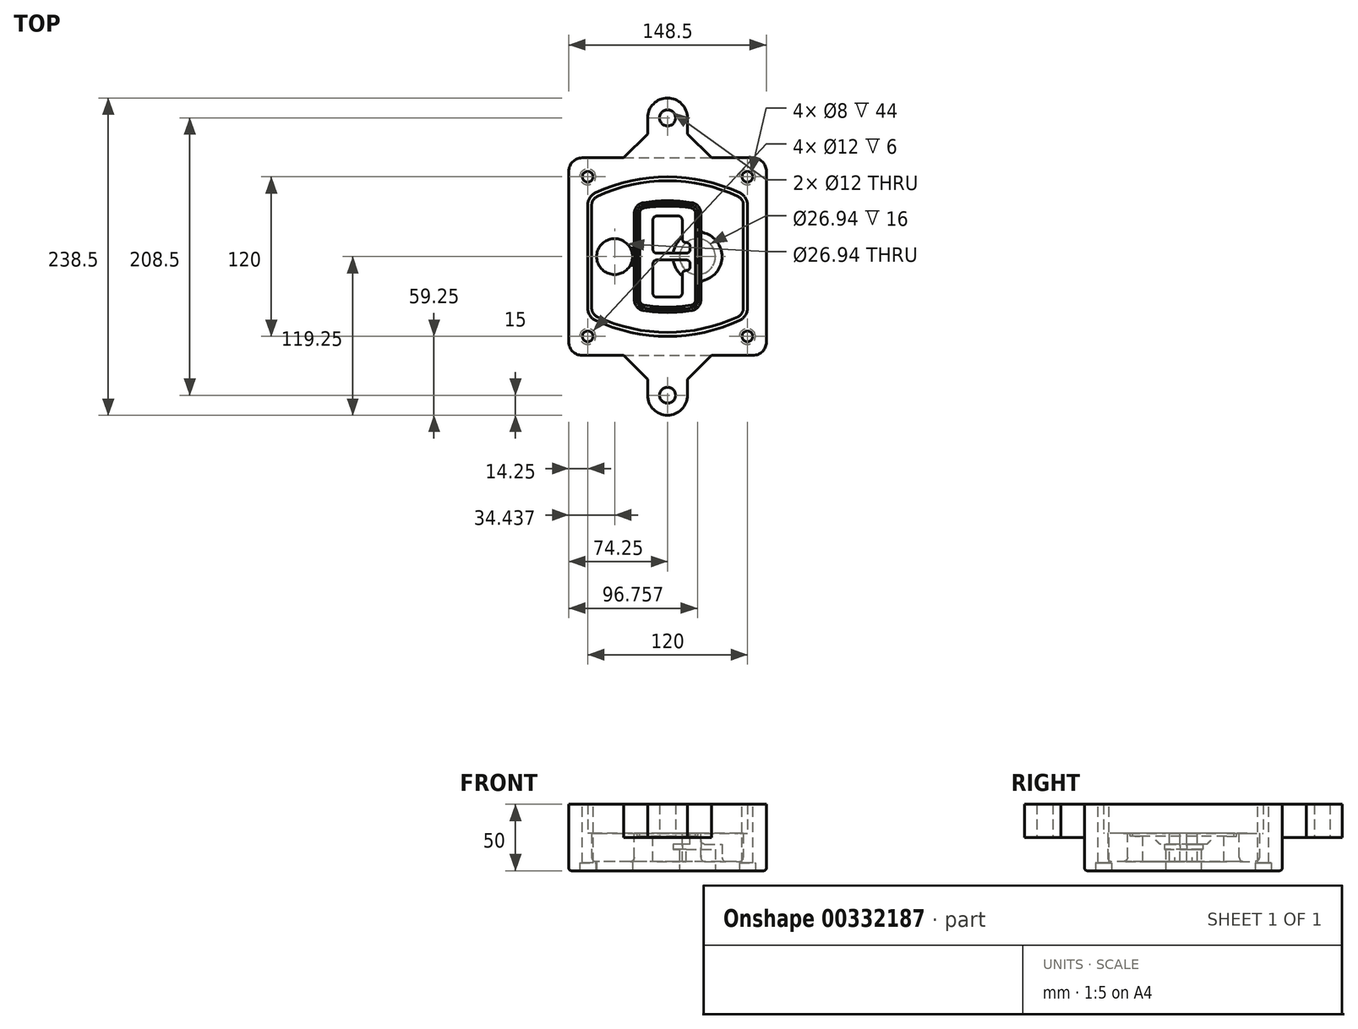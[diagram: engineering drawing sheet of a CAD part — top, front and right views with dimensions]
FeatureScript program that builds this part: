
annotation { "Feature Type Name" : "Feature", "Feature Type Description" : "" }
export const myFeature = defineFeature(function(context is Context, id is Id, definition is map)
    precondition{}
    {
        {
            var Q0;
            Q0=qCreatedBy(makeId("Top.planeOp"),FACE);
            var sketch = newSketch(context, id + "F0", { "sketchPlane" : qUnion([Q0])});
            skPoint(sketch, "E0.rect.middle", {"position": v(0, 0) * mm});
            skLineSegment(sketch, "E1.bottom", {"start": v(-64.25, -74.25) * mm, "end": v(64.25, -74.25) * mm});
            skLineSegment(sketch, "E1.top", {"start": v(-64.25, 74.25) * mm, "end": v(64.25, 74.25) * mm});
            skLineSegment(sketch, "E1.left", {"start": v(-74.25, -64.25) * mm, "end": v(-74.25, 64.25) * mm});
            skLineSegment(sketch, "E1.right", {"start": v(74.25, -64.25) * mm, "end": v(74.25, 64.25) * mm});
            skLineSegment(sketch, "E2", {"start": v(-74.25, 74.25) * mm, "end": v(74.25, -74.25) * mm, "construction": true});
            skLineSegment(sketch, "E3", {"start": v(74.25, 74.25) * mm, "end": v(-74.25, -74.25) * mm, "construction": true});
            skCircle(sketch, "E4", {"center": v(-60, 60) * mm, "radius": 4 * mm});
            skCircle(sketch, "E5", {"center": v(60, 60) * mm, "radius": 4 * mm});
            skCircle(sketch, "E6", {"center": v(60, -60) * mm, "radius": 4 * mm});
            skCircle(sketch, "E7", {"center": v(-60, -60) * mm, "radius": 4 * mm});
            skLineSegment(sketch, "E8", {"start": v(-60, 60) * mm, "end": v(60, 60) * mm, "construction": true});
            skLineSegment(sketch, "E9", {"start": v(60, 60) * mm, "end": v(60, -60) * mm, "construction": true});
            skLineSegment(sketch, "E10", {"start": v(60, -60) * mm, "end": v(-60, -60) * mm, "construction": true});
            skLineSegment(sketch, "E11", {"start": v(-60, -60) * mm, "end": v(-60, 60) * mm, "construction": true});
            skLineSegment(sketch, "E12", {"start": v(-60, 38.83) * mm, "end": v(-60, -38.83) * mm});
            skLineSegment(sketch, "E13", {"start": v(60, 38.83) * mm, "end": v(60, -38.83) * mm});
            skArc(sketch, "E14", {"start": v(54.26, 47.88) * mm, "mid": v(0, 60) * mm, "end": v(-54.26, 47.88) * mm});
            skArc(sketch, "E15", {"start": v(-54.26, -47.88) * mm, "mid": v(0, -60) * mm, "end": v(54.26, -47.88) * mm});
            skLineSegment(sketch, "E16", {"start": v(-60, 0) * mm, "end": v(60, 0) * mm, "construction": true});
            skPoint(sketch, "E17.visualSharp", {"position": v(-60, -45) * mm});
            skArc(sketch, "E17.filletArc", {"start": v(-60, -38.83) * mm, "mid": v(-58.44, -44.2) * mm, "end": v(-54.26, -47.88) * mm});
            skPoint(sketch, "E18.visualSharp", {"position": v(-60, 45) * mm});
            skArc(sketch, "E18.filletArc", {"start": v(-54.26, 47.88) * mm, "mid": v(-58.44, 44.2) * mm, "end": v(-60, 38.83) * mm});
            skPoint(sketch, "E19.visualSharp", {"position": v(60, 45) * mm});
            skArc(sketch, "E19.filletArc", {"start": v(60, 38.83) * mm, "mid": v(58.44, 44.2) * mm, "end": v(54.26, 47.88) * mm});
            skPoint(sketch, "E20.visualSharp", {"position": v(60, -45) * mm});
            skArc(sketch, "E20.filletArc", {"start": v(54.26, -47.88) * mm, "mid": v(58.44, -44.2) * mm, "end": v(60, -38.83) * mm});
            skPoint(sketch, "E21.visualSharp", {"position": v(-74.25, 74.25) * mm});
            skArc(sketch, "E21.filletArc", {"start": v(-64.25, 74.25) * mm, "mid": v(-71.32, 71.32) * mm, "end": v(-74.25, 64.25) * mm});
            skPoint(sketch, "E22.visualSharp", {"position": v(74.25, 74.25) * mm});
            skArc(sketch, "E22.filletArc", {"start": v(74.25, 64.25) * mm, "mid": v(71.32, 71.32) * mm, "end": v(64.25, 74.25) * mm});
            skPoint(sketch, "E23.visualSharp", {"position": v(74.25, -74.25) * mm});
            skArc(sketch, "E23.filletArc", {"start": v(64.25, -74.25) * mm, "mid": v(71.32, -71.32) * mm, "end": v(74.25, -64.25) * mm});
            skPoint(sketch, "E24.visualSharp", {"position": v(-74.25, -74.25) * mm});
            skArc(sketch, "E24.filletArc", {"start": v(-74.25, -64.25) * mm, "mid": v(-71.32, -71.32) * mm, "end": v(-64.25, -74.25) * mm});
            skArc(sketch, "E25.0", {"start": v(57, 38.83) * mm, "mid": v(55.9, 42.58) * mm, "end": v(52.98, 45.17) * mm});
            skLineSegment(sketch, "E25.1", {"start": v(57, 38.83) * mm, "end": v(57, -38.83) * mm});
            skArc(sketch, "E25.2", {"start": v(52.98, -45.17) * mm, "mid": v(55.9, -42.58) * mm, "end": v(57, -38.83) * mm});
            skArc(sketch, "E25.3", {"start": v(-52.98, -45.17) * mm, "mid": v(0, -57) * mm, "end": v(52.98, -45.17) * mm});
            skArc(sketch, "E25.4", {"start": v(-57, -38.83) * mm, "mid": v(-55.9, -42.58) * mm, "end": v(-52.98, -45.17) * mm});
            skArc(sketch, "E25.5", {"start": v(52.98, 45.17) * mm, "mid": v(0, 57) * mm, "end": v(-52.98, 45.17) * mm});
            skLineSegment(sketch, "E25.6", {"start": v(-57, 38.83) * mm, "end": v(-57, -38.83) * mm});
            skArc(sketch, "E25.7", {"start": v(-52.98, 45.17) * mm, "mid": v(-55.9, 42.58) * mm, "end": v(-57, 38.83) * mm});
            skArc(sketch, "E26.0", {"start": v(-55.96, 51.5) * mm, "mid": v(-61.82, 46.33) * mm, "end": v(-64, 38.83) * mm});
            skArc(sketch, "E26.1", {"start": v(55.96, 51.5) * mm, "mid": v(0, 64) * mm, "end": v(-55.96, 51.5) * mm});
            skArc(sketch, "E26.2", {"start": v(64, 38.83) * mm, "mid": v(61.82, 46.33) * mm, "end": v(55.96, 51.5) * mm});
            skLineSegment(sketch, "E26.3", {"start": v(64, 38.83) * mm, "end": v(64, -38.83) * mm});
            skArc(sketch, "E26.4", {"start": v(55.96, -51.5) * mm, "mid": v(61.82, -46.33) * mm, "end": v(64, -38.83) * mm});
            skLineSegment(sketch, "E26.5", {"start": v(-64, 38.83) * mm, "end": v(-64, -38.83) * mm});
            skArc(sketch, "E26.6", {"start": v(-55.96, -51.5) * mm, "mid": v(0, -64) * mm, "end": v(55.96, -51.5) * mm});
            skArc(sketch, "E26.7", {"start": v(-64, -38.83) * mm, "mid": v(-61.82, -46.33) * mm, "end": v(-55.96, -51.5) * mm});
            skSolve(sketch);
        }
        {
            var Q0;
            Q0=makeQuery(id+"F0.imprint","IMPRINT",FACE,{"disambiguationData":[TD([[makeQuery(id+"F0.imprint","IMPRINT",EDGE,{"derivedFrom":sQuery(id+"F0.wireOp",EDGE,"E1.bottom")}),1.0]])]});
            var Q1;
            Q1=makeQuery(id+"F0.imprint","IMPRINT",FACE,{"disambiguationData":[TD([[makeQuery(id+"F0.imprint","IMPRINT",EDGE,{"derivedFrom":sQuery(id+"F0.wireOp",EDGE,"E12")}),1.0]])]});
            var Q2;
            Q2=makeQuery(id+"F0.imprint","IMPRINT",FACE,{"disambiguationData":[TD([[makeQuery(id+"F0.imprint","IMPRINT",EDGE,{"derivedFrom":sQuery(id+"F0.wireOp",EDGE,"E25.0")}),1.0]])]});
            var Q3;
            Q3=makeQuery(id+"F0.imprint","IMPRINT",FACE,{"disambiguationData":[TD([[makeQuery(id+"F0.imprint","IMPRINT",EDGE,{"derivedFrom":sQuery(id+"F0.wireOp",EDGE,"E12")}),-1.0]])]});
            extrude(context, id + "F1", {"entities" : qUnion([Q0, Q1, Q2, Q3]), "oppositeDirection" : true, "depth" : 25 * mm});
        }
        {
            var Q0;
            Q0=makeQuery(id+"F0.imprint","IMPRINT",FACE,{"disambiguationData":[TD([[makeQuery(id+"F0.imprint","IMPRINT",EDGE,{"derivedFrom":sQuery(id+"F0.wireOp",EDGE,"E12")}),1.0]])]});
            extrude(context, id + "F2", {"entities" : qUnion([Q0]), "operationType" : NewBodyOperationType.ADD, "depth" : 3 * mm});
        }
        {
            var Q0;
            Q0=makeQuery(id+"F0.imprint","IMPRINT",FACE,{"disambiguationData":[TD([[makeQuery(id+"F0.imprint","IMPRINT",EDGE,{"derivedFrom":sQuery(id+"F0.wireOp",EDGE,"E25.0")}),1.0]])]});
            extrude(context, id + "F3", {"entities" : qUnion([Q0]), "operationType" : NewBodyOperationType.REMOVE, "oppositeDirection" : true, "depth" : 18 * mm});
        }
        {
            var Q0;
            Q0=makeQuery(id+"F2.opExtrude","CAP_FACE",FACE,{"disambiguationData":[OSD([sQuery(id+"F0.wireOp",EDGE,"E12"),sQuery(id+"F0.wireOp",EDGE,"E13"),sQuery(id+"F0.wireOp",EDGE,"E14"),sQuery(id+"F0.wireOp",EDGE,"E15"),sQuery(id+"F0.wireOp",EDGE,"E17.filletArc"),sQuery(id+"F0.wireOp",EDGE,"E18.filletArc"),sQuery(id+"F0.wireOp",EDGE,"E19.filletArc"),sQuery(id+"F0.wireOp",EDGE,"E20.filletArc"),sQuery(id+"F0.wireOp",EDGE,"E25.0"),sQuery(id+"F0.wireOp",EDGE,"E25.1"),sQuery(id+"F0.wireOp",EDGE,"E25.2"),sQuery(id+"F0.wireOp",EDGE,"E25.3"),sQuery(id+"F0.wireOp",EDGE,"E25.4"),sQuery(id+"F0.wireOp",EDGE,"E25.5"),sQuery(id+"F0.wireOp",EDGE,"E25.6"),sQuery(id+"F0.wireOp",EDGE,"E25.7")])],"isStart":false});
            var sketch = newSketch(context, id + "F4", { "sketchPlane" : qUnion([Q0])});
            skArc(sketch, "E27.0", {"start": v(-18.34, -40.45) * mm, "mid": v(0, -42) * mm, "end": v(18.34, -40.45) * mm});
            skArc(sketch, "E28.0", {"start": v(18.34, 40.45) * mm, "mid": v(0, 42) * mm, "end": v(-18.34, 40.45) * mm});
            skLineSegment(sketch, "E29", {"start": v(-25, 32.57) * mm, "end": v(-25, -32.57) * mm});
            skLineSegment(sketch, "E30", {"start": v(25, 32.57) * mm, "end": v(25, -32.57) * mm});
            skLineSegment(sketch, "E31", {"start": v(-25, 39.1) * mm, "end": v(25, 39.1) * mm, "construction": true});
            skLineSegment(sketch, "E32", {"start": v(-25, -39.1) * mm, "end": v(25, -39.1) * mm, "construction": true});
            skPoint(sketch, "E33.visualSharp", {"position": v(-25, 39.1) * mm});
            skArc(sketch, "E33.filletArc", {"start": v(-18.34, 40.45) * mm, "mid": v(-23.11, 37.73) * mm, "end": v(-25, 32.57) * mm});
            skPoint(sketch, "E34.visualSharp", {"position": v(25, 39.1) * mm});
            skArc(sketch, "E34.filletArc", {"start": v(25, 32.57) * mm, "mid": v(23.11, 37.73) * mm, "end": v(18.34, 40.45) * mm});
            skPoint(sketch, "E35.visualSharp", {"position": v(25, -39.1) * mm});
            skArc(sketch, "E35.filletArc", {"start": v(18.34, -40.45) * mm, "mid": v(23.11, -37.73) * mm, "end": v(25, -32.57) * mm});
            skPoint(sketch, "E36.visualSharp", {"position": v(-25, -39.1) * mm});
            skArc(sketch, "E36.filletArc", {"start": v(-25, -32.57) * mm, "mid": v(-23.11, -37.73) * mm, "end": v(-18.34, -40.45) * mm});
            skArc(sketch, "E37.0", {"start": v(52.98, 45.17) * mm, "mid": v(0, 57) * mm, "end": v(-52.98, 45.17) * mm});
            skArc(sketch, "E37.1", {"start": v(-52.98, 45.17) * mm, "mid": v(-55.9, 42.58) * mm, "end": v(-57, 38.83) * mm});
            skLineSegment(sketch, "E37.2", {"start": v(-57, 38.83) * mm, "end": v(-57, -38.83) * mm});
            skArc(sketch, "E37.3", {"start": v(-57, -38.83) * mm, "mid": v(-55.9, -42.58) * mm, "end": v(-52.98, -45.17) * mm});
            skArc(sketch, "E37.4", {"start": v(-52.98, -45.17) * mm, "mid": v(0, -57) * mm, "end": v(52.98, -45.17) * mm});
            skArc(sketch, "E37.5", {"start": v(52.98, -45.17) * mm, "mid": v(55.9, -42.58) * mm, "end": v(57, -38.83) * mm});
            skLineSegment(sketch, "E37.6", {"start": v(57, 38.83) * mm, "end": v(57, -38.83) * mm});
            skArc(sketch, "E37.7", {"start": v(57, 38.83) * mm, "mid": v(55.9, 42.58) * mm, "end": v(52.98, 45.17) * mm});
            skLineSegment(sketch, "E38.0", {"start": v(23, 32.57) * mm, "end": v(23, -32.57) * mm});
            skArc(sketch, "E38.1", {"start": v(18, -38.48) * mm, "mid": v(21.58, -36.44) * mm, "end": v(23, -32.57) * mm});
            skArc(sketch, "E38.2", {"start": v(-18, -38.48) * mm, "mid": v(0, -40) * mm, "end": v(18, -38.48) * mm});
            skArc(sketch, "E38.3", {"start": v(-23, -32.57) * mm, "mid": v(-21.58, -36.44) * mm, "end": v(-18, -38.48) * mm});
            skLineSegment(sketch, "E38.4", {"start": v(-23, 32.57) * mm, "end": v(-23, -32.57) * mm});
            skArc(sketch, "E38.5", {"start": v(23, 32.57) * mm, "mid": v(21.58, 36.44) * mm, "end": v(18, 38.48) * mm});
            skArc(sketch, "E38.6", {"start": v(-18, 38.48) * mm, "mid": v(-21.58, 36.44) * mm, "end": v(-23, 32.57) * mm});
            skArc(sketch, "E38.7", {"start": v(18, 38.48) * mm, "mid": v(0, 40) * mm, "end": v(-18, 38.48) * mm});
            skArc(sketch, "E39.0", {"start": v(21, 32.57) * mm, "mid": v(20.06, 35.15) * mm, "end": v(17.67, 36.5) * mm});
            skLineSegment(sketch, "E39.1", {"start": v(21, 32.57) * mm, "end": v(21, -32.57) * mm});
            skArc(sketch, "E39.2", {"start": v(17.67, -36.5) * mm, "mid": v(20.06, -35.15) * mm, "end": v(21, -32.57) * mm});
            skArc(sketch, "E39.3", {"start": v(-17.67, -36.5) * mm, "mid": v(0, -38) * mm, "end": v(17.67, -36.5) * mm});
            skArc(sketch, "E39.4", {"start": v(-21, -32.57) * mm, "mid": v(-20.06, -35.15) * mm, "end": v(-17.67, -36.5) * mm});
            skArc(sketch, "E39.5", {"start": v(17.67, 36.5) * mm, "mid": v(0, 38) * mm, "end": v(-17.67, 36.5) * mm});
            skLineSegment(sketch, "E39.6", {"start": v(-21, 32.57) * mm, "end": v(-21, -32.57) * mm});
            skArc(sketch, "E39.7", {"start": v(-17.67, 36.5) * mm, "mid": v(-20.06, 35.15) * mm, "end": v(-21, 32.57) * mm});
            skLineSegment(sketch, "E40", {"start": v(-25, 0) * mm, "end": v(25, 0) * mm, "construction": true});
            skLineSegment(sketch, "E41", {"start": v(-11, 5.5) * mm, "end": v(-11, 27.5) * mm});
            skLineSegment(sketch, "E42", {"start": v(-8, 30.5) * mm, "end": v(8, 30.5) * mm});
            skLineSegment(sketch, "E43", {"start": v(11, 27.5) * mm, "end": v(11, 13.5) * mm});
            skLineSegment(sketch, "E44", {"start": v(14, 10.5) * mm, "end": v(14, 10.5) * mm});
            skLineSegment(sketch, "E45", {"start": v(17, 7.5) * mm, "end": v(17, 5.5) * mm});
            skLineSegment(sketch, "E46", {"start": v(14, 2.5) * mm, "end": v(-8, 2.5) * mm});
            skPoint(sketch, "E47.visualSharp", {"position": v(-11, 30.5) * mm});
            skArc(sketch, "E47.filletArc", {"start": v(-8, 30.5) * mm, "mid": v(-10.12, 29.62) * mm, "end": v(-11, 27.5) * mm});
            skPoint(sketch, "E48.visualSharp", {"position": v(11, 30.5) * mm});
            skArc(sketch, "E48.filletArc", {"start": v(11, 27.5) * mm, "mid": v(10.12, 29.62) * mm, "end": v(8, 30.5) * mm});
            skPoint(sketch, "E49.visualSharp", {"position": v(11, 10.5) * mm});
            skArc(sketch, "E49.filletArc", {"start": v(11, 13.5) * mm, "mid": v(11.88, 11.38) * mm, "end": v(14, 10.5) * mm});
            skPoint(sketch, "E50.visualSharp", {"position": v(17, 10.5) * mm});
            skArc(sketch, "E50.filletArc", {"start": v(17, 7.5) * mm, "mid": v(16.12, 9.62) * mm, "end": v(14, 10.5) * mm});
            skPoint(sketch, "E51.visualSharp", {"position": v(17, 2.5) * mm});
            skArc(sketch, "E51.filletArc", {"start": v(14, 2.5) * mm, "mid": v(16.12, 3.38) * mm, "end": v(17, 5.5) * mm});
            skPoint(sketch, "E52.visualSharp", {"position": v(-11, 2.5) * mm});
            skArc(sketch, "E52.filletArc", {"start": v(-11, 5.5) * mm, "mid": v(-10.12, 3.38) * mm, "end": v(-8, 2.5) * mm});
            skLineSegment(sketch, "E53.0.MirrorCS", {"start": v(14, -2.5) * mm, "end": v(-8, -2.5) * mm});
            skArc(sketch, "E54.0.MirrorCS", {"start": v(-11, -5.5) * mm, "mid": v(-10.12, -3.38) * mm, "end": v(-8, -2.5) * mm});
            skLineSegment(sketch, "E55.0.MirrorCS", {"start": v(-11, -5.5) * mm, "end": v(-11, -27.5) * mm});
            skArc(sketch, "E56.0.MirrorCS", {"start": v(-8, -30.5) * mm, "mid": v(-10.12, -29.62) * mm, "end": v(-11, -27.5) * mm});
            skLineSegment(sketch, "E57.0.MirrorCS", {"start": v(-8, -30.5) * mm, "end": v(8, -30.5) * mm});
            skArc(sketch, "E58.0.MirrorCS", {"start": v(11, -27.5) * mm, "mid": v(10.12, -29.62) * mm, "end": v(8, -30.5) * mm});
            skLineSegment(sketch, "E59.0.MirrorCS", {"start": v(11, -27.5) * mm, "end": v(11, -13.5) * mm});
            skArc(sketch, "E60.0.MirrorCS", {"start": v(11, -13.5) * mm, "mid": v(11.88, -11.38) * mm, "end": v(14, -10.5) * mm});
            skArc(sketch, "E61.0.MirrorCS", {"start": v(17, -7.5) * mm, "mid": v(16.12, -9.62) * mm, "end": v(14, -10.5) * mm});
            skLineSegment(sketch, "E62.0.MirrorCS", {"start": v(17, -7.5) * mm, "end": v(17, -5.5) * mm});
            skArc(sketch, "E63.0.MirrorCS", {"start": v(14, -2.5) * mm, "mid": v(16.12, -3.38) * mm, "end": v(17, -5.5) * mm});
            skSolve(sketch);
        }
        {
            var Q0;
            Q0=makeQuery(id+"F4.imprint","IMPRINT",FACE,{"disambiguationData":[TD([[makeQuery(id+"F4.imprint","IMPRINT",EDGE,{"derivedFrom":sQuery(id+"F4.wireOp",EDGE,"E27.0")}),1.0]])]});
            var Q1;
            Q1=makeQuery(id+"F4.imprint","IMPRINT",FACE,{"disambiguationData":[TD([[makeQuery(id+"F4.imprint","IMPRINT",EDGE,{"derivedFrom":sQuery(id+"F4.wireOp",EDGE,"E38.0")}),-1.0]])]});
            var Q2;
            Q2=makeQuery(id+"F4.imprint","IMPRINT",FACE,{"disambiguationData":[TD([[makeQuery(id+"F4.imprint","IMPRINT",EDGE,{"derivedFrom":sQuery(id+"F4.wireOp",EDGE,"E39.0")}),1.0]])]});
            extrude(context, id + "F5", {"entities" : qUnion([Q0, Q1, Q2]), "operationType" : NewBodyOperationType.ADD, "endBound" : BoundingType.UP_TO_NEXT, "oppositeDirection" : true, "depth" : 25 * mm});
        }
        {
            var Q0;
            Q0=makeQuery(id+"F4.imprint","IMPRINT",FACE,{"disambiguationData":[TD([[makeQuery(id+"F4.imprint","IMPRINT",EDGE,{"derivedFrom":sQuery(id+"F4.wireOp",EDGE,"E38.0")}),-1.0]])]});
            extrude(context, id + "F6", {"entities" : qUnion([Q0]), "operationType" : NewBodyOperationType.REMOVE, "oppositeDirection" : true, "depth" : 2 * mm});
        }
        {
            var Q0;
            Q0=makeQuery(id+"F1.opExtrude","CAP_FACE",FACE,{"disambiguationData":[OSD([sQuery(id+"F0.wireOp",EDGE,"E1.bottom"),sQuery(id+"F0.wireOp",EDGE,"E1.top"),sQuery(id+"F0.wireOp",EDGE,"E1.left"),sQuery(id+"F0.wireOp",EDGE,"E1.right"),sQuery(id+"F0.wireOp",EDGE,"E4"),sQuery(id+"F0.wireOp",EDGE,"E5"),sQuery(id+"F0.wireOp",EDGE,"E6"),sQuery(id+"F0.wireOp",EDGE,"E7"),sQuery(id+"F0.wireOp",EDGE,"E21.filletArc"),sQuery(id+"F0.wireOp",EDGE,"E22.filletArc"),sQuery(id+"F0.wireOp",EDGE,"E23.filletArc"),sQuery(id+"F0.wireOp",EDGE,"E24.filletArc")])],"isStart":false});
            var sketch = newSketch(context, id + "F7", { "sketchPlane" : qUnion([Q0])});
            skCircle(sketch, "E64", {"center": v(22.5, 0) * mm, "radius": 13.47 * mm});
            skCircle(sketch, "E65", {"center": v(-39.81, 0) * mm, "radius": 13.47 * mm});
            skLineSegment(sketch, "E66", {"start": v(74.25, 0) * mm, "end": v(-74.25, 0) * mm});
            skCircle(sketch, "E67", {"center": v(22.5, 0) * mm, "radius": 18.47 * mm});
            skCircle(sketch, "E68", {"center": v(60, -60) * mm, "radius": 6 * mm});
            skCircle(sketch, "E69", {"center": v(-60, -60) * mm, "radius": 6 * mm});
            skCircle(sketch, "E70", {"center": v(-60, 60) * mm, "radius": 6 * mm});
            skCircle(sketch, "E71", {"center": v(60, 60) * mm, "radius": 6 * mm});
            skSolve(sketch);
        }
        {
            var Q0;
            {var subQ1=sQuery(id+"F7.wireOp",EDGE,"E66");var subQ4=sQuery(id+"F7.wireOp",EDGE,"E64");var subQ6=makeQuery(id+"F7.imprint","INTERSECT",VERTEX,{"disambiguationData":[OD(0.0)],"derivedFrom":[subQ4,subQ1]});Q0=makeQuery(id+"F7.imprint","IMPRINT",FACE,{"disambiguationData":[TD([[makeQuery(id+"F7.imprint","IMPRINT",EDGE,{"disambiguationData":[TD([[subQ6,-1.0]])],"derivedFrom":subQ4}),-1.0]])]});}
            var Q1;
            {var subQ0=sQuery(id+"F7.wireOp",EDGE,"E66");var subQ1=sQuery(id+"F7.wireOp",EDGE,"E64");var subQ3=makeQuery(id+"F7.imprint","INTERSECT",VERTEX,{"disambiguationData":[OD(0.0)],"derivedFrom":[subQ1,subQ0]});Q1=makeQuery(id+"F7.imprint","IMPRINT",FACE,{"disambiguationData":[TD([[makeQuery(id+"F7.imprint","IMPRINT",EDGE,{"disambiguationData":[TD([[subQ3,-1.0]])],"derivedFrom":subQ1}),1.0]])]});}
            var Q2;
            {var subQ0=sQuery(id+"F7.wireOp",EDGE,"E66");var subQ1=sQuery(id+"F7.wireOp",EDGE,"E64");var subQ3=makeQuery(id+"F7.imprint","INTERSECT",VERTEX,{"disambiguationData":[OD(0.0)],"derivedFrom":[subQ1,subQ0]});Q2=makeQuery(id+"F7.imprint","IMPRINT",FACE,{"disambiguationData":[TD([[makeQuery(id+"F7.imprint","IMPRINT",EDGE,{"disambiguationData":[TD([[subQ3,1.0]])],"derivedFrom":subQ1}),1.0]])]});}
            var Q3;
            {var subQ1=sQuery(id+"F7.wireOp",EDGE,"E66");var subQ4=sQuery(id+"F7.wireOp",EDGE,"E64");var subQ6=makeQuery(id+"F7.imprint","INTERSECT",VERTEX,{"disambiguationData":[OD(0.0)],"derivedFrom":[subQ4,subQ1]});Q3=makeQuery(id+"F7.imprint","IMPRINT",FACE,{"disambiguationData":[TD([[makeQuery(id+"F7.imprint","IMPRINT",EDGE,{"disambiguationData":[TD([[subQ6,1.0]])],"derivedFrom":subQ4}),-1.0]])]});}
            extrude(context, id + "F8", {"entities" : qUnion([Q0, Q1, Q2, Q3]), "operationType" : NewBodyOperationType.ADD, "oppositeDirection" : true, "depth" : 20 * mm});
        }
        {
            var Q0;
            {var subQ0=sQuery(id+"F7.wireOp",EDGE,"E66");var subQ1=sQuery(id+"F7.wireOp",EDGE,"E64");var subQ3=makeQuery(id+"F7.imprint","INTERSECT",VERTEX,{"disambiguationData":[OD(0.0)],"derivedFrom":[subQ1,subQ0]});Q0=makeQuery(id+"F7.imprint","IMPRINT",FACE,{"disambiguationData":[TD([[makeQuery(id+"F7.imprint","IMPRINT",EDGE,{"disambiguationData":[TD([[subQ3,-1.0]])],"derivedFrom":subQ1}),1.0]])]});}
            var Q1;
            {var subQ0=sQuery(id+"F7.wireOp",EDGE,"E66");var subQ1=sQuery(id+"F7.wireOp",EDGE,"E64");var subQ3=makeQuery(id+"F7.imprint","INTERSECT",VERTEX,{"disambiguationData":[OD(0.0)],"derivedFrom":[subQ1,subQ0]});Q1=makeQuery(id+"F7.imprint","IMPRINT",FACE,{"disambiguationData":[TD([[makeQuery(id+"F7.imprint","IMPRINT",EDGE,{"disambiguationData":[TD([[subQ3,1.0]])],"derivedFrom":subQ1}),1.0]])]});}
            extrude(context, id + "F9", {"entities" : qUnion([Q0, Q1]), "operationType" : NewBodyOperationType.REMOVE, "oppositeDirection" : true, "depth" : 16 * mm});
        }
        {
            var Q0;
            {var subQ0=sQuery(id+"F7.wireOp",EDGE,"E66");var subQ1=sQuery(id+"F7.wireOp",EDGE,"E65");var subQ3=makeQuery(id+"F7.imprint","INTERSECT",VERTEX,{"disambiguationData":[OD(0.0)],"derivedFrom":[subQ1,subQ0]});Q0=makeQuery(id+"F7.imprint","IMPRINT",FACE,{"disambiguationData":[TD([[makeQuery(id+"F7.imprint","IMPRINT",EDGE,{"disambiguationData":[TD([[subQ3,-1.0]])],"derivedFrom":subQ1}),1.0]])]});}
            var Q1;
            {var subQ0=sQuery(id+"F7.wireOp",EDGE,"E66");var subQ1=sQuery(id+"F7.wireOp",EDGE,"E65");var subQ3=makeQuery(id+"F7.imprint","INTERSECT",VERTEX,{"disambiguationData":[OD(0.0)],"derivedFrom":[subQ1,subQ0]});Q1=makeQuery(id+"F7.imprint","IMPRINT",FACE,{"disambiguationData":[TD([[makeQuery(id+"F7.imprint","IMPRINT",EDGE,{"disambiguationData":[TD([[subQ3,1.0]])],"derivedFrom":subQ1}),1.0]])]});}
            extrude(context, id + "F10", {"entities" : qUnion([Q0, Q1]), "operationType" : NewBodyOperationType.REMOVE, "oppositeDirection" : true, "depth" : 25 * mm});
        }
        {
            var Q0;
            Q0=makeQuery(id+"F7.imprint","IMPRINT",FACE,{"disambiguationData":[TD([[makeQuery(id+"F7.imprint","IMPRINT",EDGE,{"derivedFrom":sQuery(id+"F7.wireOp",EDGE,"E68")}),1.0]])]});
            var Q1;
            Q1=makeQuery(id+"F7.imprint","IMPRINT",FACE,{"disambiguationData":[TD([[makeQuery(id+"F7.imprint","IMPRINT",EDGE,{"derivedFrom":makeQuery(id+"F1.opExtrude","CAP_EDGE",EDGE,{"disambiguationData":[OSD([sQuery(id+"F0.wireOp",EDGE,"E5")])],"isStart":false})}),-1.0]])]});
            var Q2;
            Q2=makeQuery(id+"F7.imprint","IMPRINT",FACE,{"disambiguationData":[TD([[makeQuery(id+"F7.imprint","IMPRINT",EDGE,{"derivedFrom":sQuery(id+"F7.wireOp",EDGE,"E69")}),1.0]])]});
            var Q3;
            Q3=makeQuery(id+"F7.imprint","IMPRINT",FACE,{"disambiguationData":[TD([[makeQuery(id+"F7.imprint","IMPRINT",EDGE,{"derivedFrom":makeQuery(id+"F1.opExtrude","CAP_EDGE",EDGE,{"disambiguationData":[OSD([sQuery(id+"F0.wireOp",EDGE,"E4")])],"isStart":false})}),-1.0]])]});
            var Q4;
            Q4=makeQuery(id+"F7.imprint","IMPRINT",FACE,{"disambiguationData":[TD([[makeQuery(id+"F7.imprint","IMPRINT",EDGE,{"derivedFrom":sQuery(id+"F7.wireOp",EDGE,"E70")}),1.0]])]});
            var Q5;
            Q5=makeQuery(id+"F7.imprint","IMPRINT",FACE,{"disambiguationData":[TD([[makeQuery(id+"F7.imprint","IMPRINT",EDGE,{"derivedFrom":makeQuery(id+"F1.opExtrude","CAP_EDGE",EDGE,{"disambiguationData":[OSD([sQuery(id+"F0.wireOp",EDGE,"E7")])],"isStart":false})}),-1.0]])]});
            var Q6;
            Q6=makeQuery(id+"F7.imprint","IMPRINT",FACE,{"disambiguationData":[TD([[makeQuery(id+"F7.imprint","IMPRINT",EDGE,{"derivedFrom":sQuery(id+"F7.wireOp",EDGE,"E71")}),1.0]])]});
            var Q7;
            Q7=makeQuery(id+"F7.imprint","IMPRINT",FACE,{"disambiguationData":[TD([[makeQuery(id+"F7.imprint","IMPRINT",EDGE,{"derivedFrom":makeQuery(id+"F1.opExtrude","CAP_EDGE",EDGE,{"disambiguationData":[OSD([sQuery(id+"F0.wireOp",EDGE,"E6")])],"isStart":false})}),-1.0]])]});
            extrude(context, id + "F11", {"entities" : qUnion([Q0, Q1, Q2, Q3, Q4, Q5, Q6, Q7]), "operationType" : NewBodyOperationType.REMOVE, "oppositeDirection" : true, "depth" : 6 * mm});
        }
        {
            var Q0;
            Q0=makeQuery(id+"F9.boolean.opBoolean","COPY",FACE,{"derivedFrom":makeQuery(id+"F9.opExtrude","CAP_FACE",FACE,{"disambiguationData":[OSD([sQuery(id+"F7.wireOp",EDGE,"E64")])],"isStart":false})});
            var sketch = newSketch(context, id + "F12", { "sketchPlane" : qUnion([Q0])});
            skArc(sketch, "E72.0", {"start": v(11, 14.45) * mm, "mid": v(6.45, 9.13) * mm, "end": v(4.2, 2.5) * mm});
            skArc(sketch, "E72.1", {"start": v(4.2, -2.5) * mm, "mid": v(6.45, -9.13) * mm, "end": v(11, -14.45) * mm});
            skLineSegment(sketch, "E73", {"start": v(4.2, -2.5) * mm, "end": v(14, -2.5) * mm});
            skLineSegment(sketch, "E74.0", {"start": v(14, 2.5) * mm, "end": v(4.2, 2.5) * mm});
            skArc(sketch, "E74.1", {"start": v(14, 2.5) * mm, "mid": v(16.12, 3.38) * mm, "end": v(17, 5.5) * mm});
            skLineSegment(sketch, "E74.2", {"start": v(17, 7.5) * mm, "end": v(17, 5.5) * mm});
            skArc(sketch, "E74.3", {"start": v(17, 7.5) * mm, "mid": v(16.12, 9.62) * mm, "end": v(14, 10.5) * mm});
            skArc(sketch, "E74.4", {"start": v(11, 13.5) * mm, "mid": v(11.88, 11.38) * mm, "end": v(14, 10.5) * mm});
            skLineSegment(sketch, "E74.5", {"start": v(11, 14.45) * mm, "end": v(11, 13.5) * mm});
            skLineSegment(sketch, "E74.7", {"start": v(14, -2.5) * mm, "end": v(4.2, -2.5) * mm});
            skArc(sketch, "E74.8", {"start": v(14, -2.5) * mm, "mid": v(16.12, -3.38) * mm, "end": v(17, -5.5) * mm});
            skLineSegment(sketch, "E74.9", {"start": v(17, -7.5) * mm, "end": v(17, -5.5) * mm});
            skArc(sketch, "E74.10", {"start": v(17, -7.5) * mm, "mid": v(16.12, -9.62) * mm, "end": v(14, -10.5) * mm});
            skArc(sketch, "E74.11", {"start": v(11, -13.5) * mm, "mid": v(11.88, -11.38) * mm, "end": v(14, -10.5) * mm});
            skLineSegment(sketch, "E74.12", {"start": v(11, -14.45) * mm, "end": v(11, -13.5) * mm});
            skPoint(sketch, "E75.orphan", {"position": v(11, -27.5) * mm});
            skPoint(sketch, "E76.orphan", {"position": v(-8, -2.5) * mm});
            skPoint(sketch, "E77.orphan", {"position": v(-8, 2.5) * mm});
            skPoint(sketch, "E78.orphan", {"position": v(11, 27.5) * mm});
            skSolve(sketch);
        }
        {
            var Q0;
            {var subQ7=sQuery(id+"F12.wireOp",EDGE,"E72.0");var subQ14=sQuery(id+"F12.wireOp",EDGE,"E72.1");var subQ16=sQuery(id+"F12.wireOp",EDGE,"E74.1");var subQ18=sQuery(id+"F12.wireOp",EDGE,"E74.8");Q0=qUnion([makeQuery(id+"F12.imprint","IMPRINT",FACE,{"disambiguationData":[TD([[makeQuery(id+"F12.imprint","IMPRINT",EDGE,{"derivedFrom":subQ7}),1.0]])]}),makeQuery(id+"F12.imprint","IMPRINT",FACE,{"disambiguationData":[TD([[makeQuery(id+"F12.imprint","IMPRINT",EDGE,{"derivedFrom":subQ14}),1.0]])]}),makeQuery(id+"F12.imprint","IMPRINT",FACE,{"disambiguationData":[TD([[makeQuery(id+"F12.imprint","IMPRINT",EDGE,{"derivedFrom":subQ16}),1.0]])]}),makeQuery(id+"F12.imprint","IMPRINT",FACE,{"disambiguationData":[TD([[makeQuery(id+"F12.imprint","IMPRINT",EDGE,{"derivedFrom":subQ18}),-1.0]])]})]);}
            var Q1;
            Q1=makeQuery(id+"F5.boolean.opBoolean","SPLIT",FACE,{"disambiguationData":[TD([makeQuery(id+"F5.opExtrude","SWEPT_FACE",FACE,{"disambiguationData":[OSD([sQuery(id+"F4.wireOp",EDGE,"E41")])]})])],"derivedFrom":makeQuery(id+"F3.boolean.opBoolean","COPY",FACE,{"derivedFrom":makeQuery(id+"F3.opExtrude","CAP_FACE",FACE,{"disambiguationData":[OSD([sQuery(id+"F0.wireOp",EDGE,"E25.0"),sQuery(id+"F0.wireOp",EDGE,"E25.1"),sQuery(id+"F0.wireOp",EDGE,"E25.2"),sQuery(id+"F0.wireOp",EDGE,"E25.3"),sQuery(id+"F0.wireOp",EDGE,"E25.4"),sQuery(id+"F0.wireOp",EDGE,"E25.5"),sQuery(id+"F0.wireOp",EDGE,"E25.6"),sQuery(id+"F0.wireOp",EDGE,"E25.7")])],"isStart":false})})});
            extrude(context, id + "F13", {"entities" : qUnion([Q0]), "operationType" : NewBodyOperationType.REMOVE, "endBound" : BoundingType.UP_TO_SURFACE, "endBoundEntityFace" : qUnion([Q1]), "depth" : 25 * mm});
        }
        {
            var Q0;
            Q0=makeQuery(id+"F3.boolean.opBoolean","COPY",EDGE,{"derivedFrom":makeQuery(id+"F3.opExtrude","CAP_EDGE",EDGE,{"disambiguationData":[OSD([sQuery(id+"F0.wireOp",EDGE,"E25.6")])],"isStart":false})});
            var Q1;
            Q1=makeQuery(id+"F8.boolean.opBoolean","INTERSECT",EDGE,{"derivedFrom":[makeQuery(id+"F5.opExtrude","SWEPT_FACE",FACE,{"disambiguationData":[OSD([sQuery(id+"F4.wireOp",EDGE,"E30")])]}),makeQuery(id+"F8.opExtrude","CAP_FACE",FACE,{"disambiguationData":[OSD([sQuery(id+"F7.wireOp",EDGE,"E67")])],"isStart":false})]});
            var Q2;
            Q2=makeQuery(id+"F8.boolean.opBoolean","INTERSECT",EDGE,{"disambiguationData":[OD(1.0)],"derivedFrom":[makeQuery(id+"F5.opExtrude","SWEPT_FACE",FACE,{"disambiguationData":[OSD([sQuery(id+"F4.wireOp",EDGE,"E30")])]}),makeQuery(id+"F8.opExtrude","SWEPT_FACE",FACE,{"disambiguationData":[OSD([sQuery(id+"F7.wireOp",EDGE,"E67")])]})]});
            var Q3;
            {var subQ0=sQuery(id+"F4.wireOp",EDGE,"E30");Q3=makeQuery(id+"F8.boolean.opBoolean","SPLIT",EDGE,{"disambiguationData":[TD([makeQuery(id+"F5.opExtrude","SWEPT_FACE",FACE,{"disambiguationData":[OSD([sQuery(id+"F4.wireOp",EDGE,"E35.filletArc")])]})])],"derivedFrom":makeQuery(id+"F5.opExtrude","CAP_EDGE",EDGE,{"disambiguationData":[OSD([subQ0])],"isStart":false})});}
            var Q4;
            {var subQ0=sQuery(id+"F0.wireOp",EDGE,"E25.7");var subQ1=sQuery(id+"F0.wireOp",EDGE,"E25.1");var subQ2=sQuery(id+"F0.wireOp",EDGE,"E25.6");var subQ3=sQuery(id+"F0.wireOp",EDGE,"E25.5");var subQ4=sQuery(id+"F0.wireOp",EDGE,"E25.4");var subQ5=sQuery(id+"F0.wireOp",EDGE,"E25.0");var subQ6=sQuery(id+"F0.wireOp",EDGE,"E25.2");var subQ7=sQuery(id+"F0.wireOp",EDGE,"E25.3");Q4=makeQuery(id+"F8.boolean.opBoolean","INTERSECT",EDGE,{"derivedFrom":[makeQuery(id+"F5.boolean.opBoolean","SPLIT",FACE,{"disambiguationData":[TD([makeQuery(id+"F2.opExtrude","SWEPT_FACE",FACE,{"disambiguationData":[OSD([subQ5])]})])],"derivedFrom":makeQuery(id+"F3.boolean.opBoolean","COPY",FACE,{"derivedFrom":makeQuery(id+"F3.opExtrude","CAP_FACE",FACE,{"disambiguationData":[OSD([subQ5,subQ1,subQ6,subQ7,subQ4,subQ3,subQ2,subQ0])],"isStart":false})})}),makeQuery(id+"F8.opExtrude","SWEPT_FACE",FACE,{"disambiguationData":[OSD([sQuery(id+"F7.wireOp",EDGE,"E67")])]})]});}
            var Q5;
            Q5=makeQuery(id+"F8.boolean.opBoolean","INTERSECT",EDGE,{"disambiguationData":[OD(0.0)],"derivedFrom":[makeQuery(id+"F5.opExtrude","SWEPT_FACE",FACE,{"disambiguationData":[OSD([sQuery(id+"F4.wireOp",EDGE,"E30")])]}),makeQuery(id+"F8.opExtrude","SWEPT_FACE",FACE,{"disambiguationData":[OSD([sQuery(id+"F7.wireOp",EDGE,"E67")])]})]});
            fillet(context, id + "F14", {"entities" : qUnion([Q0, Q1, Q2, Q3, Q4, Q5]), "radius" : 3 * mm, "tangentPropagation" : true, "allowEdgeOverflow" : false});
        }
        {
            var Q0;
            Q0=makeQuery(id+"F1.opExtrude","CAP_EDGE",EDGE,{"disambiguationData":[OSD([sQuery(id+"F0.wireOp",EDGE,"E1.bottom")])],"isStart":false});
            fillet(context, id + "F15", {"entities" : qUnion([Q0]), "radius" : 2 * mm, "tangentPropagation" : true, "allowEdgeOverflow" : false});
        }
        {
            var Q0;
            {var subQ0=sQuery(id+"F0.wireOp",EDGE,"E21.filletArc");var subQ1=sQuery(id+"F0.wireOp",EDGE,"E7");var subQ2=sQuery(id+"F0.wireOp",EDGE,"E6");var subQ3=sQuery(id+"F0.wireOp",EDGE,"E5");var subQ4=sQuery(id+"F0.wireOp",EDGE,"E4");var subQ5=sQuery(id+"F0.wireOp",EDGE,"E22.filletArc");var subQ6=sQuery(id+"F0.wireOp",EDGE,"E1.bottom");var subQ7=sQuery(id+"F0.wireOp",EDGE,"E1.right");var subQ8=sQuery(id+"F0.wireOp",EDGE,"E1.top");var subQ9=sQuery(id+"F0.wireOp",EDGE,"E1.left");var subQ10=sQuery(id+"F0.wireOp",EDGE,"E23.filletArc");var subQ11=sQuery(id+"F0.wireOp",EDGE,"E24.filletArc");Q0=makeQuery(id+"F2.boolean.opBoolean","SPLIT",FACE,{"disambiguationData":[TD([makeQuery(id+"F1.opExtrude","SWEPT_FACE",FACE,{"disambiguationData":[OSD([subQ6])]})])],"derivedFrom":makeQuery(id+"F1.opExtrude","CAP_FACE",FACE,{"disambiguationData":[OSD([subQ6,subQ8,subQ9,subQ7,subQ4,subQ3,subQ2,subQ1,subQ0,subQ5,subQ10,subQ11])],"isStart":true})});}
            var sketch = newSketch(context, id + "F16", { "sketchPlane" : qUnion([Q0])});
            skLineSegment(sketch, "E79", {"start": v(0, 74.25) * mm, "end": v(0, 104.25) * mm, "construction": true});
            skCircle(sketch, "E80", {"center": v(0, 104.25) * mm, "radius": 6 * mm});
            skLineSegment(sketch, "E81", {"start": v(-15, 104.25) * mm, "end": v(-15, 92.25) * mm});
            skLineSegment(sketch, "E82", {"start": v(-15, 92.25) * mm, "end": v(-33, 74.25) * mm});
            skLineSegment(sketch, "E83", {"start": v(15, 104.25) * mm, "end": v(15, 92.25) * mm});
            skLineSegment(sketch, "E84", {"start": v(15, 92.25) * mm, "end": v(33, 74.25) * mm});
            skArc(sketch, "E85", {"start": v(15, 104.25) * mm, "mid": v(0, 119.25) * mm, "end": v(-15, 104.25) * mm});
            skLineSegment(sketch, "E86", {"start": v(-74.25, 0) * mm, "end": v(74.25, 0) * mm, "construction": true});
            skLineSegment(sketch, "E87.MirrorCS", {"start": v(15, -92.25) * mm, "end": v(33, -74.25) * mm});
            skLineSegment(sketch, "E88.MirrorCS", {"start": v(15, -104.25) * mm, "end": v(15, -92.25) * mm});
            skArc(sketch, "E89.MirrorCS", {"start": v(15, -104.25) * mm, "mid": v(0, -119.25) * mm, "end": v(-15, -104.25) * mm});
            skCircle(sketch, "E90.MirrorC", {"center": v(0, -104.25) * mm, "radius": 6 * mm});
            skLineSegment(sketch, "E91.MirrorCS", {"start": v(0, -74.25) * mm, "end": v(0, -104.25) * mm, "construction": true});
            skLineSegment(sketch, "E92.MirrorCS", {"start": v(-15, -92.25) * mm, "end": v(-33, -74.25) * mm});
            skLineSegment(sketch, "E93.MirrorCS", {"start": v(-15, -104.25) * mm, "end": v(-15, -92.25) * mm});
            skSolve(sketch);
        }
        {
            var Q0;
            Q0=makeQuery(id+"F16.imprint","IMPRINT",FACE,{"disambiguationData":[TD([[makeQuery(id+"F16.imprint","IMPRINT",EDGE,{"derivedFrom":makeQuery(id+"F1.opExtrude","CAP_EDGE",EDGE,{"disambiguationData":[OSD([sQuery(id+"F0.wireOp",EDGE,"E1.left")])],"isStart":true})}),-1.0]])]});
            var Q1;
            Q1=makeQuery(id+"F16.imprint","IMPRINT",FACE,{"disambiguationData":[TD([[makeQuery(id+"F16.imprint","IMPRINT",EDGE,{"derivedFrom":sQuery(id+"F16.wireOp",EDGE,"E80")}),-1.0]])]});
            var Q2;
            {var subQ0=sQuery(id+"F16.wireOp",EDGE,"E87.MirrorCS");Q2=makeQuery(id+"F16.imprint","IMPRINT",FACE,{"disambiguationData":[TD([[makeQuery(id+"F16.imprint","IMPRINT",EDGE,{"derivedFrom":subQ0}),1.0]])]});}
            extrude(context, id + "F17", {"entities" : qUnion([Q0, Q1, Q2]), "operationType" : NewBodyOperationType.ADD, "depth" : 25 * mm});
        }
    });
